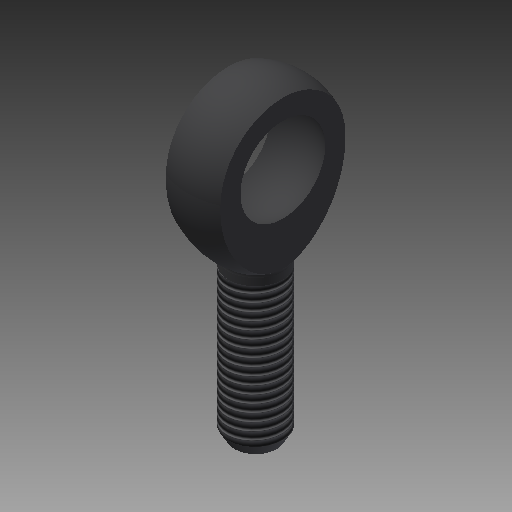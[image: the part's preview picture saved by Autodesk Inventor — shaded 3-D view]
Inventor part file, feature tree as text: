
AUTODESK INVENTOR PART (.ipt)
format: ipt  version: 2018 (Build 220112000, 112)  size: 190,976 bytes
history: native  units: mm
features: other x7, sketch x4, revolve x3, thread x1, extrude x1
ambient origin geometry x8: Origin, YZ Plane, XZ Plane, XY Plane, X Axis, Y Axis, Z Axis, Center Point
bodies: Solid1 (feature_tree)
feature tree (16):
  revolve  "Revolution1"  [1 undecoded]
  thread  "Thread1"  [1 undecoded]
  extrude  "Extrusion1"  TaperAngle=360.0deg  [1 undecoded]
  revolve  "Revolution2"  [1 undecoded]
  revolve  "Revolution3"  [1 undecoded]
  other  "IP1_XY"
  other  "IP1_YZ"
  other  "IP1_ZX"
  other  "IP1_X"
  other  "IP1_Y"
  other  "IP1_Z"
  other  "IP1_Center"
  sketch  "Sketch_5"  dims[d0=360.0deg d1=30.66mm d2=0.0mm d3=30.0mm d4=0.0mm]
  sketch  "Sketch_6"  dims[d5=360.0deg d6=360.0deg]
  sketch  "Sketch_7"
  sketch  "Sketch_14"
note: 5 required parameter values undecoded (feature->parameter linkage not recoverable at this tier; creation-order binding heuristic only, values carry confidence <= 0.55)